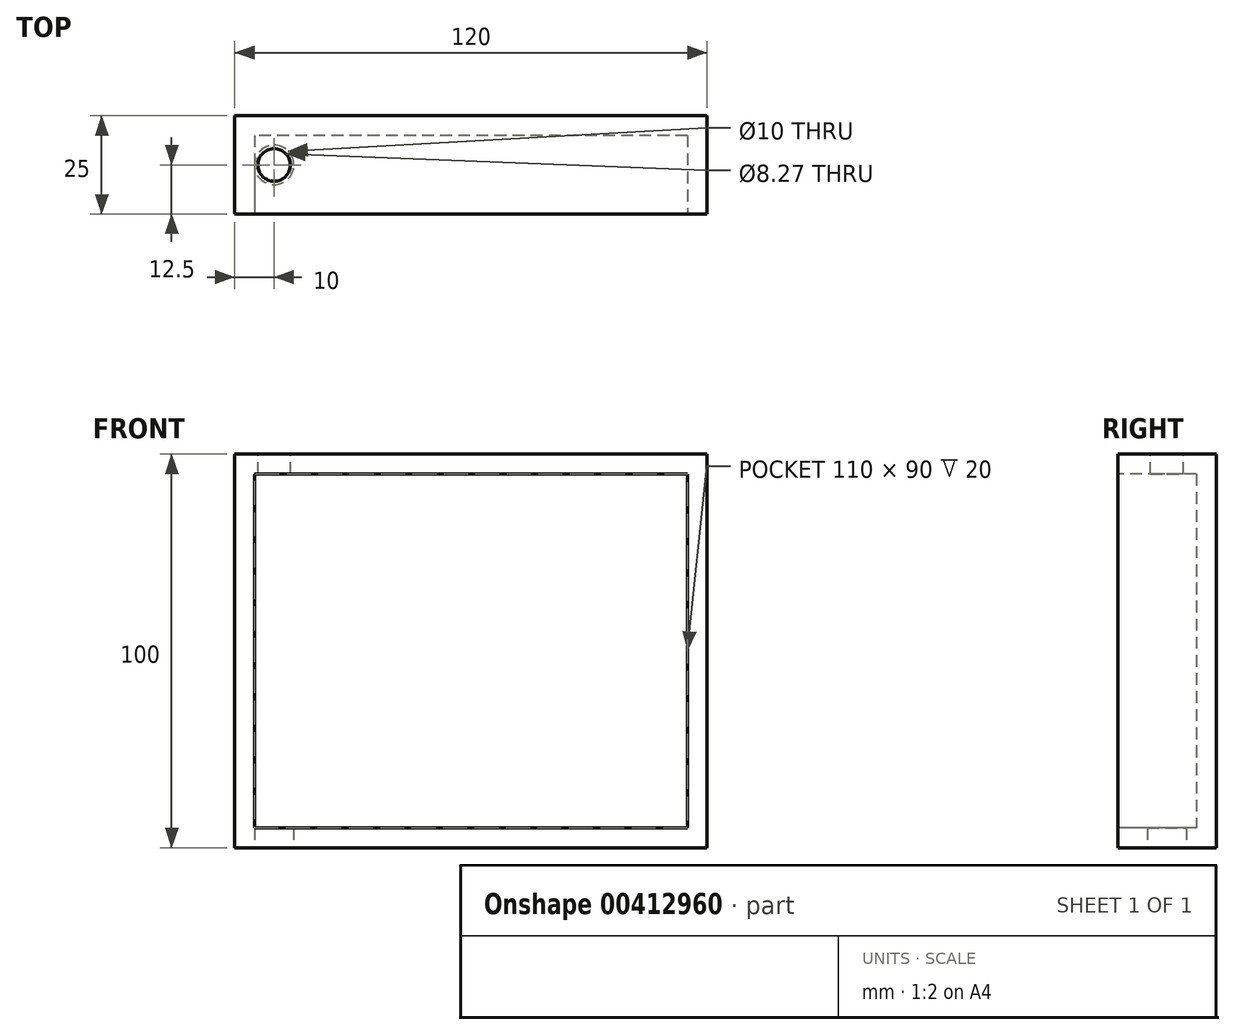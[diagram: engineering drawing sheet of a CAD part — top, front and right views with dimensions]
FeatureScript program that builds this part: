
annotation { "Feature Type Name" : "Feature", "Feature Type Description" : "" }
export const myFeature = defineFeature(function(context is Context, id is Id, definition is map)
    precondition{}
    {
        {
            var Q0;
            Q0=qCreatedBy(makeId("Front.planeOp"),FACE);
            var sketch = newSketch(context, id + "F0", { "sketchPlane" : qUnion([Q0])});
            skLineSegment(sketch, "E0.bottom", {"start": v(-60, 50) * mm, "end": v(60, 50) * mm});
            skLineSegment(sketch, "E0.top", {"start": v(-60, -50) * mm, "end": v(60, -50) * mm});
            skLineSegment(sketch, "E0.left", {"start": v(-60, 50) * mm, "end": v(-60, -50) * mm});
            skLineSegment(sketch, "E0.right", {"start": v(60, 50) * mm, "end": v(60, -50) * mm});
            skPoint(sketch, "E0.middle", {"position": v(0, 0) * mm});
            skSolve(sketch);
        }
        {
            var Q0;
            Q0=makeQuery(id+"F0.imprint","IMPRINT",FACE,{"disambiguationData":[TD([[makeQuery(id+"F0.imprint","IMPRINT",EDGE,{"derivedFrom":sQuery(id+"F0.wireOp",EDGE,"E0.bottom")}),-1.0]])]});
            extrude(context, id + "F1", {"entities" : qUnion([Q0]), "depth" : 25 * mm});
        }
        {
            var Q0;
            Q0=makeQuery(id+"F1.opExtrude","CAP_FACE",FACE,{"disambiguationData":[OSD([sQuery(id+"F0.wireOp",EDGE,"E0.bottom"),sQuery(id+"F0.wireOp",EDGE,"E0.top"),sQuery(id+"F0.wireOp",EDGE,"E0.left"),sQuery(id+"F0.wireOp",EDGE,"E0.right")])],"isStart":false});
            var sketch = newSketch(context, id + "F2", { "sketchPlane" : qUnion([Q0])});
            skLineSegment(sketch, "E1.bottom", {"start": v(55, 45) * mm, "end": v(-55, 45) * mm});
            skLineSegment(sketch, "E1.top", {"start": v(55, -45) * mm, "end": v(-55, -45) * mm});
            skLineSegment(sketch, "E1.left", {"start": v(55, 45) * mm, "end": v(55, -45) * mm});
            skLineSegment(sketch, "E1.right", {"start": v(-55, 45) * mm, "end": v(-55, -45) * mm});
            skPoint(sketch, "E1.middle", {"position": v(0, 0) * mm});
            skSolve(sketch);
        }
        {
            var Q0;
            Q0=qSketchRegion(id+"F2",true);
            extrude(context, id + "F3", {"entities" : qUnion([Q0]), "operationType" : NewBodyOperationType.REMOVE, "oppositeDirection" : true, "depth" : 20 * mm});
        }
        {
            var Q0;
            Q0=makeQuery(id+"F1.opExtrude","SWEPT_FACE",FACE,{"disambiguationData":[OSD([sQuery(id+"F0.wireOp",EDGE,"E0.top")])]});
            var sketch = newSketch(context, id + "F4", { "sketchPlane" : qUnion([Q0])});
            skCircle(sketch, "E2", {"center": v(-50, 12.5) * mm, "radius": 5 * mm});
            skPoint(sketch, "E2.centerSnap0", {"position": v(-60, 12.5) * mm});
            skSolve(sketch);
        }
        {
            var Q0;
            Q0=makeQuery(id+"F4.imprint","IMPRINT",FACE,{"disambiguationData":[TD([[makeQuery(id+"F4.imprint","IMPRINT",EDGE,{"derivedFrom":sQuery(id+"F4.wireOp",EDGE,"E2")}),1.0]])]});
            var Q1;
            Q1=makeQuery(id+"F3.boolean.opBoolean","COPY",FACE,{"derivedFrom":makeQuery(id+"F3.opExtrude","SWEPT_FACE",FACE,{"disambiguationData":[OSD([sQuery(id+"F2.wireOp",EDGE,"E1.top")])]})});
            extrude(context, id + "F5", {"entities" : qUnion([Q0, Q1]), "operationType" : NewBodyOperationType.REMOVE, "oppositeDirection" : true, "depth" : 10 * mm});
        }
        {
            var Q0;
            Q0=makeQuery(id+"F1.opExtrude","SWEPT_FACE",FACE,{"disambiguationData":[OSD([sQuery(id+"F0.wireOp",EDGE,"E0.bottom")])]});
            var sketch = newSketch(context, id + "F6", { "sketchPlane" : qUnion([Q0])});
            skCircle(sketch, "E3", {"center": v(-50, -12.5) * mm, "radius": 4.13 * mm});
            skSolve(sketch);
        }
        {
            var Q0;
            Q0=qSketchRegion(id+"F6",true);
            extrude(context, id + "F7", {"entities" : qUnion([Q0]), "operationType" : NewBodyOperationType.REMOVE, "oppositeDirection" : true, "depth" : 10 * mm});
        }
    });
